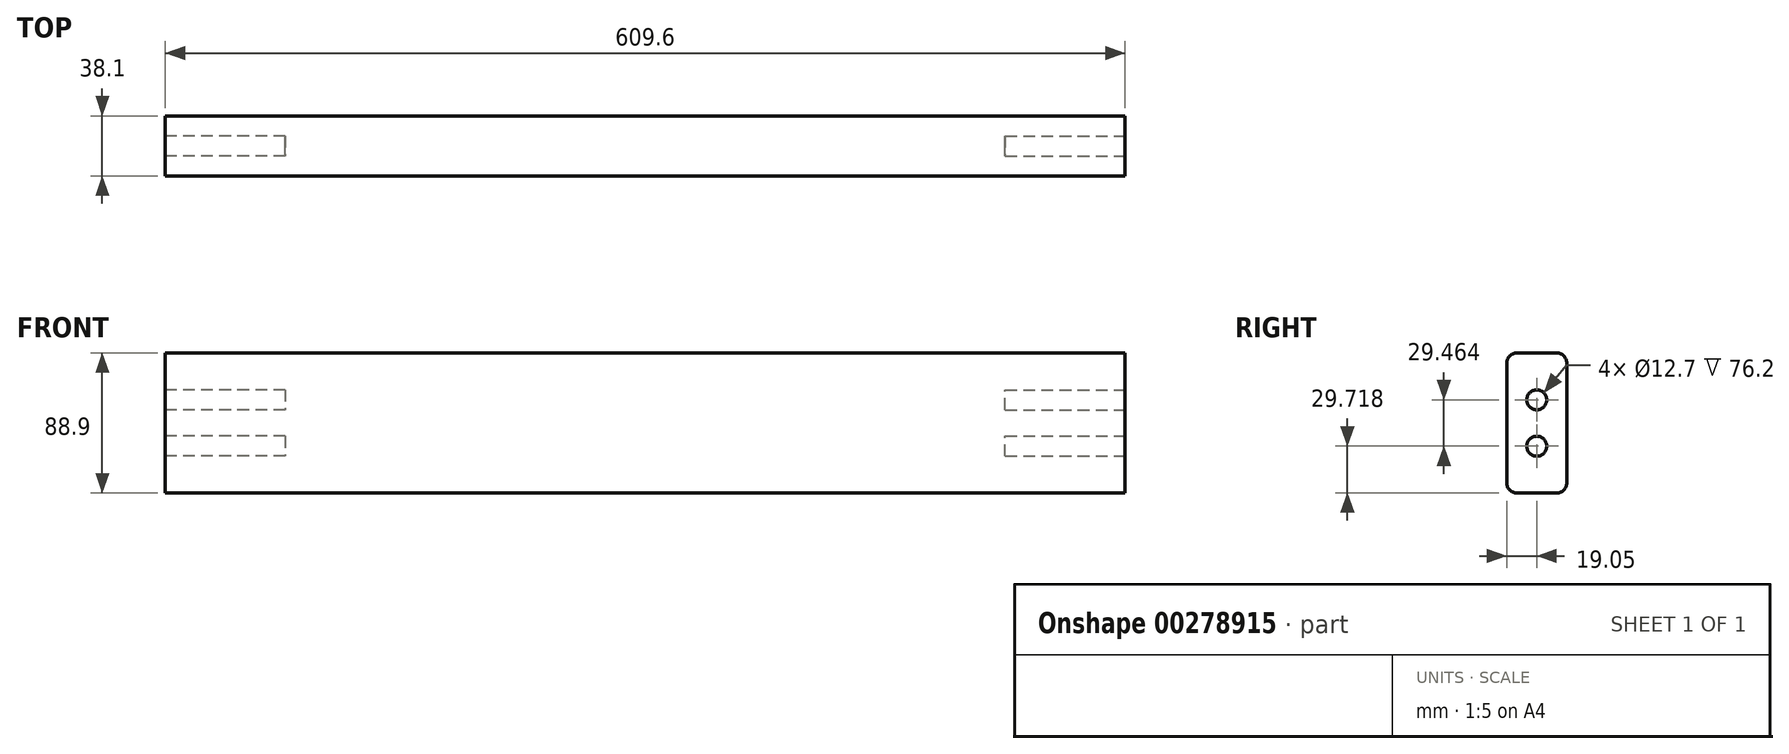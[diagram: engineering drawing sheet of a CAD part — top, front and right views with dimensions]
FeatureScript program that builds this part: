
annotation { "Feature Type Name" : "Feature", "Feature Type Description" : "" }
export const myFeature = defineFeature(function(context is Context, id is Id, definition is map)
    precondition{}
    {
        {
            var Q0;
            Q0=qCreatedBy(makeId("Front.planeOp"),FACE);
            var sketch = newSketch(context, id + "F0", { "sketchPlane" : qUnion([Q0])});
            skLineSegment(sketch, "E0.bottom", {"start": v(304.8, -67.56) * mm, "end": v(-304.8, -67.56) * mm});
            skLineSegment(sketch, "E0.top", {"start": v(304.8, 21.34) * mm, "end": v(-304.8, 21.34) * mm});
            skLineSegment(sketch, "E0.left", {"start": v(304.8, -67.56) * mm, "end": v(304.8, 21.34) * mm});
            skLineSegment(sketch, "E0.right", {"start": v(-304.8, -67.56) * mm, "end": v(-304.8, 21.34) * mm});
            skPoint(sketch, "E0.middle", {"position": v(0, -23.1) * mm});
            skSolve(sketch);
        }
        {
            var Q0;
            Q0=qSketchRegion(id+"F0",true);
            extrude(context, id + "F1", {"entities" : qUnion([Q0]), "oppositeDirection" : true, "depth" : 38.1 * mm});
        }
        {
            var Q0;
            Q0=makeQuery(id+"F1.opExtrude","SWEPT_FACE",FACE,{"disambiguationData":[OSD([sQuery(id+"F0.wireOp",EDGE,"E0.right")])]});
            var sketch = newSketch(context, id + "F2", { "sketchPlane" : qUnion([Q0])});
            skCircle(sketch, "E1", {"center": v(-19.05, -8.38) * mm, "radius": 6.35 * mm});
            skCircle(sketch, "E2.0.1.0", {"center": v(-19.05, -37.84) * mm, "radius": 6.35 * mm});
            skLineSegment(sketch, "E2.direction1", {"start": v(-19.05, -8.38) * mm, "end": v(6.35, -8.38) * mm, "construction": true});
            skLineSegment(sketch, "E2.direction2", {"start": v(-19.05, -8.38) * mm, "end": v(-19.05, -37.84) * mm, "construction": true});
            skSolve(sketch);
        }
        {
            var Q0;
            Q0=makeQuery(id+"F2.imprint","IMPRINT",FACE,{"disambiguationData":[TD([[makeQuery(id+"F2.imprint","IMPRINT",EDGE,{"derivedFrom":sQuery(id+"F2.wireOp",EDGE,"E1")}),1.0]])]});
            var Q1;
            Q1=makeQuery(id+"F2.imprint","IMPRINT",FACE,{"disambiguationData":[TD([[makeQuery(id+"F2.imprint","IMPRINT",EDGE,{"derivedFrom":sQuery(id+"F2.wireOp",EDGE,"E2.0.1.0")}),1.0]])]});
            var Q2;
            Q2=sQuery(id+"F2.wireOp",EDGE,"E2.0.1.0");
            var Q3;
            Q3=sQuery(id+"F2.wireOp",EDGE,"E1");
            extrude(context, id + "F5", {"entities" : qUnion([Q0, Q1]), "operationType" : NewBodyOperationType.REMOVE, "surfaceEntities" : qUnion([Q2, Q3]), "oppositeDirection" : true, "depth" : 76.2 * mm});
        }
        {
            var Q0;
            Q0=makeQuery(id+"F1.opExtrude","SWEPT_FACE",FACE,{"disambiguationData":[OSD([sQuery(id+"F0.wireOp",EDGE,"E0.left")])]});
            var sketch = newSketch(context, id + "F3", { "sketchPlane" : qUnion([Q0])});
            skCircle(sketch, "E3", {"center": v(19.05, -8.38) * mm, "radius": 6.35 * mm});
            skCircle(sketch, "E4.0.1.0", {"center": v(19.05, -37.84) * mm, "radius": 6.35 * mm});
            skLineSegment(sketch, "E4.direction1", {"start": v(19.05, -8.38) * mm, "end": v(44.45, -8.38) * mm, "construction": true});
            skLineSegment(sketch, "E4.direction2", {"start": v(19.05, -8.38) * mm, "end": v(19.05, -37.84) * mm, "construction": true});
            skSolve(sketch);
        }
        {
            var Q0;
            Q0=qSketchRegion(id+"F3",true);
            extrude(context, id + "F4", {"entities" : qUnion([Q0]), "operationType" : NewBodyOperationType.REMOVE, "oppositeDirection" : true, "depth" : 76.2 * mm});
        }
        {
            var Q0;
            Q0=makeQuery(id+"F1.opExtrude","CAP_EDGE",EDGE,{"disambiguationData":[OSD([sQuery(id+"F0.wireOp",EDGE,"E0.top")])],"isStart":true});
            var Q1;
            Q1=makeQuery(id+"F1.opExtrude","CAP_EDGE",EDGE,{"disambiguationData":[OSD([sQuery(id+"F0.wireOp",EDGE,"E0.top")])],"isStart":false});
            var Q2;
            Q2=makeQuery(id+"F1.opExtrude","CAP_EDGE",EDGE,{"disambiguationData":[OSD([sQuery(id+"F0.wireOp",EDGE,"E0.bottom")])],"isStart":false});
            var Q3;
            Q3=makeQuery(id+"F1.opExtrude","CAP_EDGE",EDGE,{"disambiguationData":[OSD([sQuery(id+"F0.wireOp",EDGE,"E0.bottom")])],"isStart":true});
            fillet(context, id + "F6", {"entities" : qUnion([Q0, Q1, Q2, Q3]), "radius" : 6.35 * mm, "tangentPropagation" : true, "allowEdgeOverflow" : false});
        }
    });
